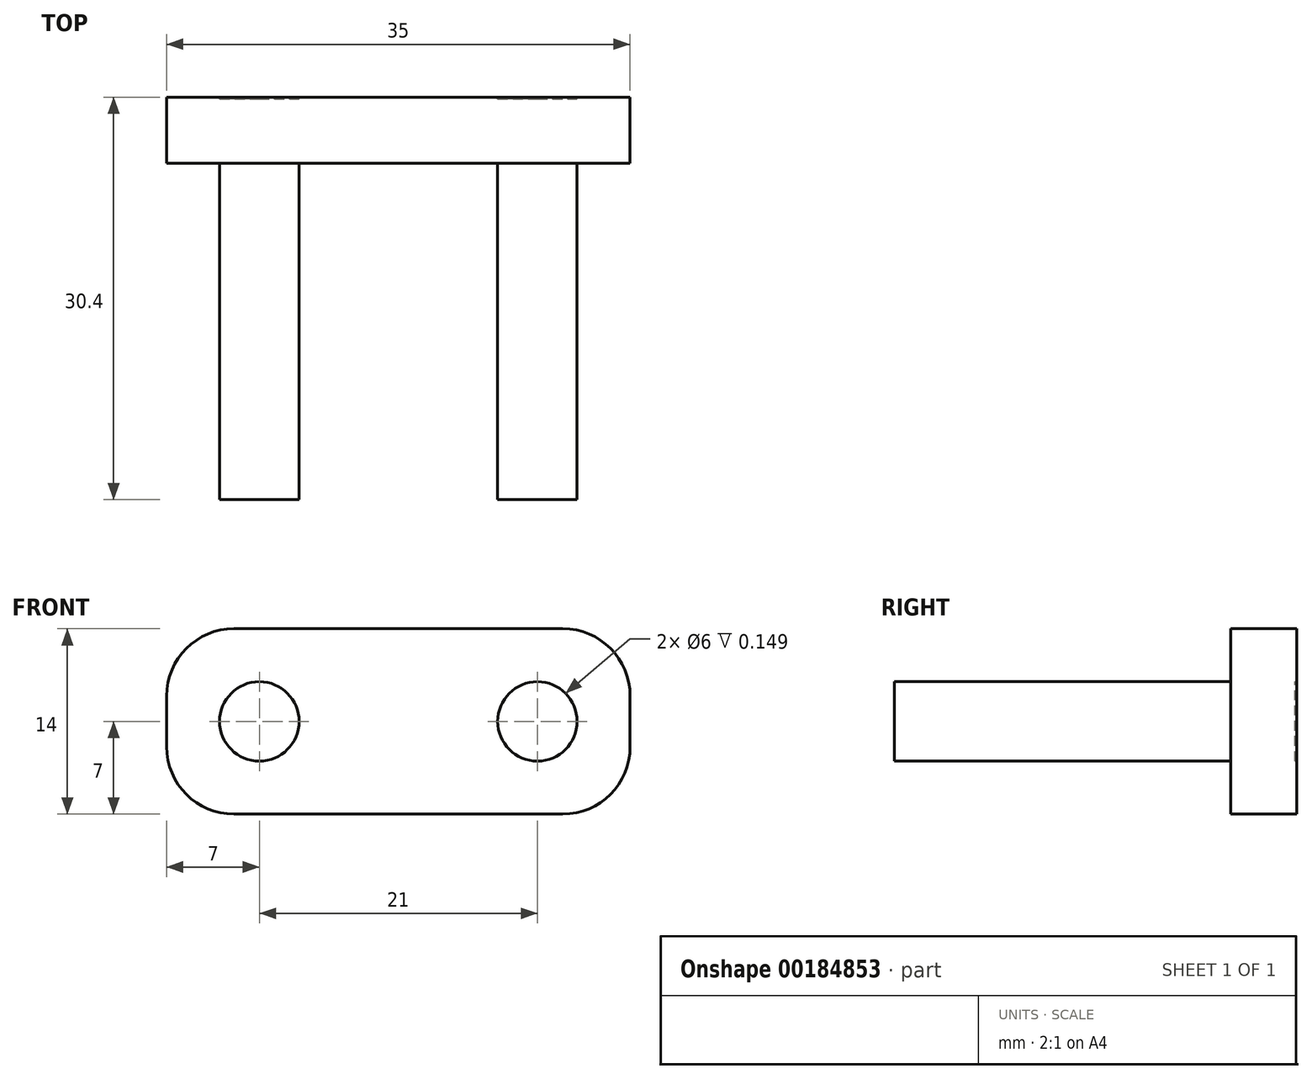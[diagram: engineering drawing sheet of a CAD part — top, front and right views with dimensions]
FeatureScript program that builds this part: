
annotation { "Feature Type Name" : "Feature", "Feature Type Description" : "" }
export const myFeature = defineFeature(function(context is Context, id is Id, definition is map)
    precondition{}
    {
        {
            var Q0;
            Q0=qCreatedBy(makeId("Front.planeOp"),FACE);
            var sketch = newSketch(context, id + "F0", { "sketchPlane" : qUnion([Q0])});
            skLineSegment(sketch, "E0.bottom", {"start": v(0, 0) * mm, "end": v(35, 0) * mm});
            skLineSegment(sketch, "E0.top", {"start": v(0, 14) * mm, "end": v(35, 14) * mm});
            skLineSegment(sketch, "E0.left", {"start": v(0, 0) * mm, "end": v(0, 14) * mm});
            skLineSegment(sketch, "E0.right", {"start": v(35, 0) * mm, "end": v(35, 14) * mm});
            skLineSegment(sketch, "E1", {"start": v(35, 7) * mm, "end": v(0, 7) * mm, "construction": true});
            skLineSegment(sketch, "E2", {"start": v(0, 7) * mm, "end": v(7, 7) * mm, "construction": true});
            skCircle(sketch, "E3", {"center": v(7, 7) * mm, "radius": 3 * mm});
            skLineSegment(sketch, "E4", {"start": v(35, 7) * mm, "end": v(28, 7) * mm, "construction": true});
            skCircle(sketch, "E5", {"center": v(28, 7) * mm, "radius": 3 * mm});
            skSolve(sketch);
        }
        {
            var Q0;
            Q0=makeQuery(id+"F0.imprint","IMPRINT",FACE,{"disambiguationData":[TD([[makeQuery(id+"F0.imprint","IMPRINT",EDGE,{"derivedFrom":sQuery(id+"F0.wireOp",EDGE,"E0.bottom")}),1.0]])]});
            extrude(context, id + "F1", {"entities" : qUnion([Q0]), "depth" : 5 * mm});
        }
        {
            var Q0;
            Q0=makeQuery(id+"F1.opExtrude","SWEPT_EDGE",EDGE,{"disambiguationData":[OSD([sQuery(id+"F0.wireOp",EDGE,"E0.top"),sQuery(id+"F0.wireOp",EDGE,"E0.right")])]});
            var Q1;
            Q1=makeQuery(id+"F1.opExtrude","SWEPT_EDGE",EDGE,{"disambiguationData":[OSD([sQuery(id+"F0.wireOp",EDGE,"E0.bottom"),sQuery(id+"F0.wireOp",EDGE,"E0.right")])]});
            var Q2;
            Q2=makeQuery(id+"F1.opExtrude","SWEPT_EDGE",EDGE,{"disambiguationData":[OSD([sQuery(id+"F0.wireOp",EDGE,"E0.bottom"),sQuery(id+"F0.wireOp",EDGE,"E0.left")])]});
            var Q3;
            Q3=makeQuery(id+"F1.opExtrude","SWEPT_EDGE",EDGE,{"disambiguationData":[OSD([sQuery(id+"F0.wireOp",EDGE,"E0.top"),sQuery(id+"F0.wireOp",EDGE,"E0.left")])]});
            fillet(context, id + "F2", {"entities" : qUnion([Q0, Q1, Q2, Q3]), "radius" : 5.08 * mm, "tangentPropagation" : true, "allowEdgeOverflow" : false});
        }
        {
            var Q0;
            Q0=makeQuery(id+"F1.opExtrude","CAP_FACE",FACE,{"disambiguationData":[OSD([sQuery(id+"F0.wireOp",EDGE,"E0.bottom"),sQuery(id+"F0.wireOp",EDGE,"E0.top"),sQuery(id+"F0.wireOp",EDGE,"E0.left"),sQuery(id+"F0.wireOp",EDGE,"E0.right"),sQuery(id+"F0.wireOp",EDGE,"E3"),sQuery(id+"F0.wireOp",EDGE,"E5")])],"isStart":false});
            var sketch = newSketch(context, id + "F3", { "sketchPlane" : qUnion([Q0])});
            skCircle(sketch, "E6.0", {"center": v(28, 7) * mm, "radius": 3 * mm});
            skCircle(sketch, "E7.0", {"center": v(7, 7) * mm, "radius": 3 * mm});
            skSolve(sketch);
        }
        {
            var Q0;
            Q0=makeQuery(id+"F3.imprint","IMPRINT",FACE,{"disambiguationData":[TD([[makeQuery(id+"F3.imprint","IMPRINT",EDGE,{"derivedFrom":sQuery(id+"F3.wireOp",EDGE,"E6.0")}),1.0]])]});
            var Q1;
            Q1=makeQuery(id+"F3.imprint","IMPRINT",FACE,{"disambiguationData":[TD([[makeQuery(id+"F3.imprint","IMPRINT",EDGE,{"derivedFrom":sQuery(id+"F3.wireOp",EDGE,"E7.0")}),1.0]])]});
            extrude(context, id + "F4", {"entities" : qUnion([Q0, Q1]), "operationType" : NewBodyOperationType.ADD, "depth" : 25.4 * mm, "hasSecondDirection" : true, "secondDirectionOppositeDirection" : true, "secondDirectionDepth" : 4.85 * mm});
        }
    });
